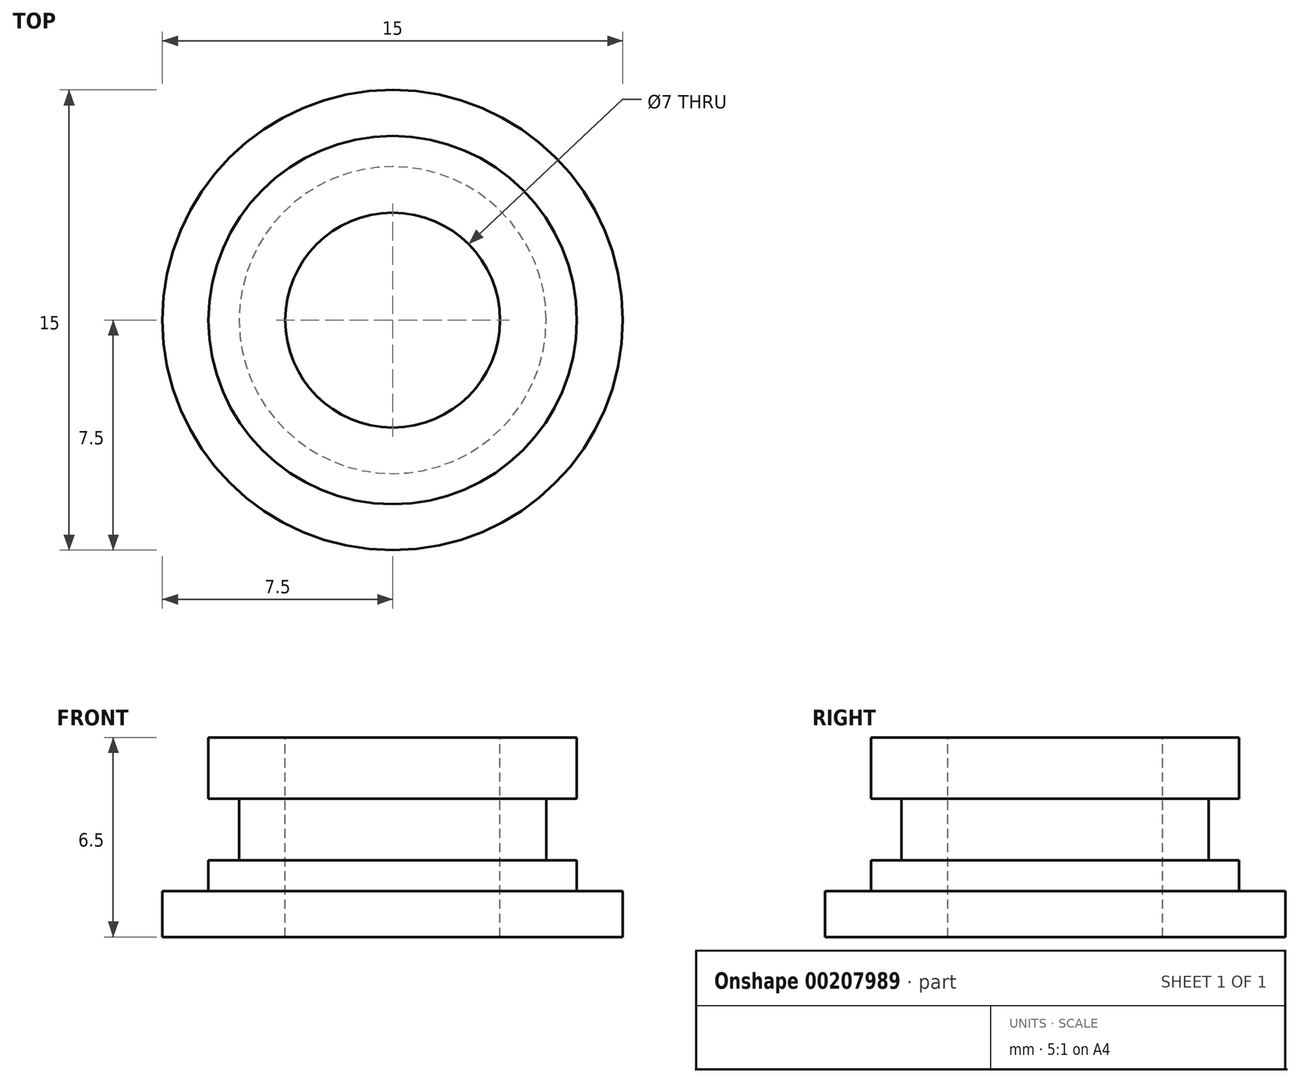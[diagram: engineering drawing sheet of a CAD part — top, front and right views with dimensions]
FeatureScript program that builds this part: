
annotation { "Feature Type Name" : "Feature", "Feature Type Description" : "" }
export const myFeature = defineFeature(function(context is Context, id is Id, definition is map)
    precondition{}
    {
        {
            var Q0;
            Q0=qCreatedBy(makeId("Front.planeOp"),FACE);
            var sketch = newSketch(context, id + "F0", { "sketchPlane" : qUnion([Q0])});
            skLineSegment(sketch, "E0", {"start": v(-7.5, 0) * mm, "end": v(-7.5, 1.5) * mm});
            skLineSegment(sketch, "E1", {"start": v(-7.5, 1.5) * mm, "end": v(-6, 1.5) * mm});
            skLineSegment(sketch, "E2", {"start": v(-6, 1.5) * mm, "end": v(-6, 2.5) * mm});
            skLineSegment(sketch, "E3", {"start": v(-6, 2.5) * mm, "end": v(-5, 2.5) * mm});
            skLineSegment(sketch, "E4", {"start": v(-5, 2.5) * mm, "end": v(-5, 4.5) * mm});
            skLineSegment(sketch, "E5", {"start": v(-5, 4.5) * mm, "end": v(-6, 4.5) * mm});
            skLineSegment(sketch, "E6", {"start": v(-6, 4.5) * mm, "end": v(-6, 6.5) * mm});
            skLineSegment(sketch, "E7", {"start": v(-6, 6.5) * mm, "end": v(-3.5, 6.5) * mm});
            skLineSegment(sketch, "E8", {"start": v(-3.5, 6.5) * mm, "end": v(-3.5, 0) * mm});
            skLineSegment(sketch, "E9", {"start": v(-7.5, 0) * mm, "end": v(-3.5, 0) * mm});
            skLineSegment(sketch, "E10", {"start": v(0, 8.47) * mm, "end": v(0, 0) * mm});
            skSolve(sketch);
        }
        {
            var Q0;
            Q0=makeQuery(id+"F0.imprint","IMPRINT",FACE,{"disambiguationData":[TD([[makeQuery(id+"F0.imprint","IMPRINT",EDGE,{"derivedFrom":sQuery(id+"F0.wireOp",EDGE,"E0")}),-1.0]])]});
            var Q1;
            Q1=sQuery(id+"F0.wireOp",EDGE,"E10");
            revolve(context, id + "F1", {"entities" : qUnion([Q0]), "axis" : qUnion([Q1]), "revolveType" : RevolveType.FULL});
        }
    });
